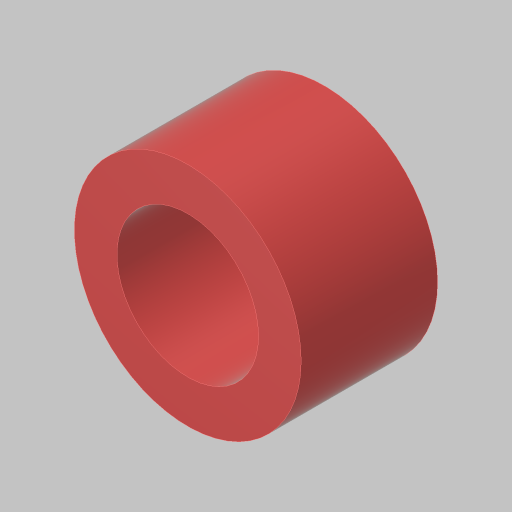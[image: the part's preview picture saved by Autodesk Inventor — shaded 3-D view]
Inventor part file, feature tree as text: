
AUTODESK INVENTOR PART (.ipt)
format: ipt  version: 2023.5 (Build 275446000, 446)  size: 115,712 bytes
history: native  units: in
note: dims shown in document units (in); Inventor stores cm internally (conversion verified against a paired STEP export)
features: extrude x1, sketch x1
ambient origin geometry x8: Origin, YZ Plane, XZ Plane, XY Plane, X Axis, Y Axis, Z Axis, Center Point
bodies: Solid1 (feature_tree)
feature tree (2):
  extrude  "Extrusion1"  Depth=0.4in
  sketch  "Sketch1"  dims[d0=0.415in d1=0.125in d2=0.4in d3=0.0in]
